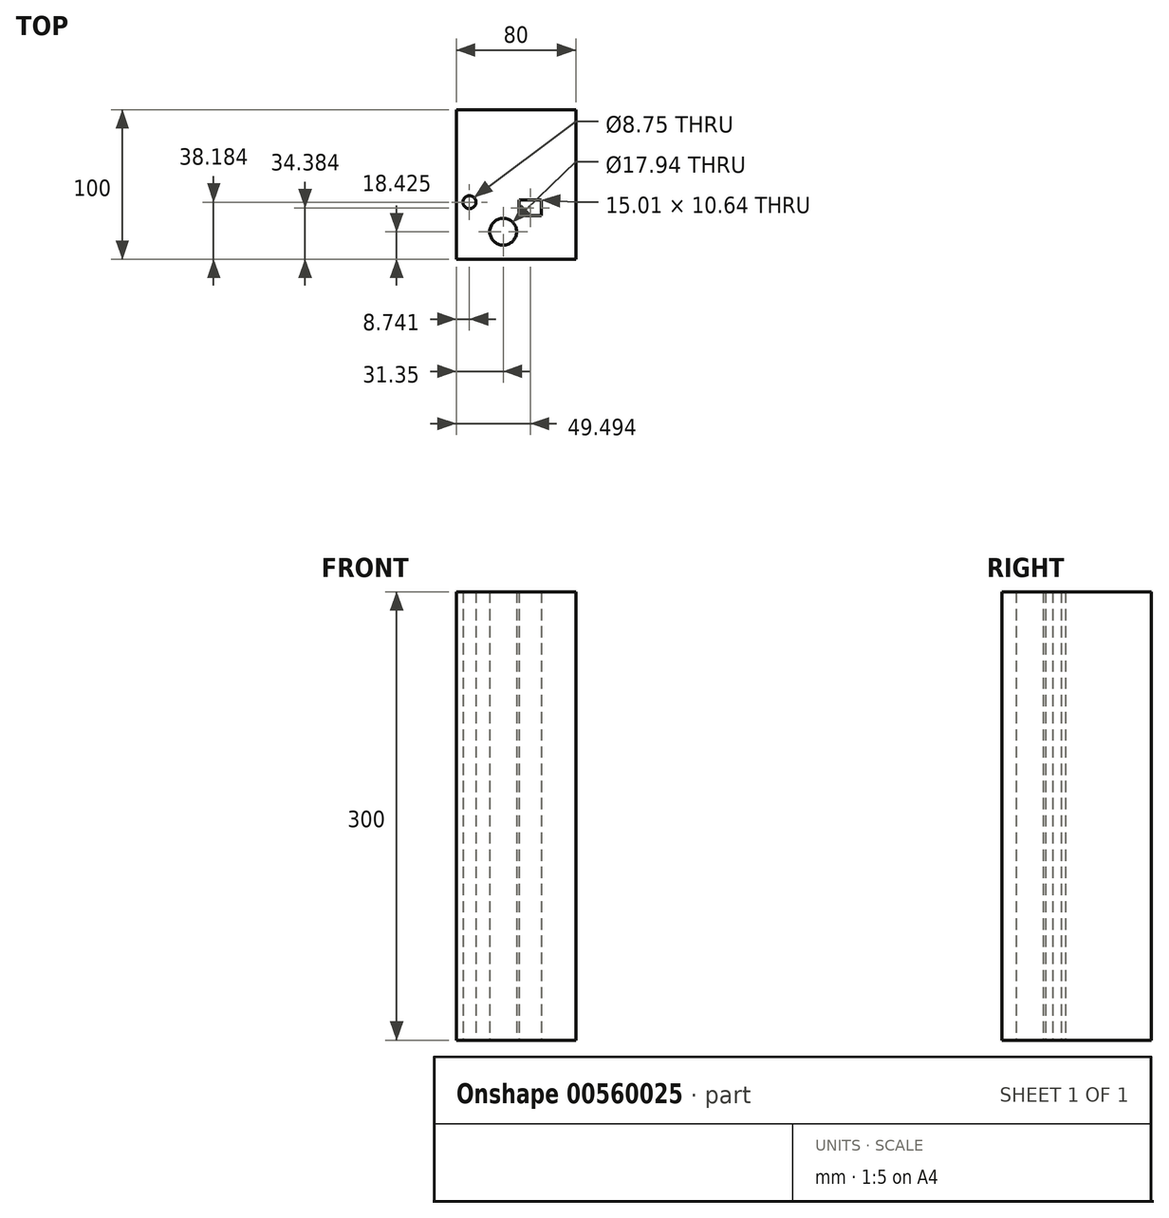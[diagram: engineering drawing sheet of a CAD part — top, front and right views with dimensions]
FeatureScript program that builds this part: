
annotation { "Feature Type Name" : "Feature", "Feature Type Description" : "" }
export const myFeature = defineFeature(function(context is Context, id is Id, definition is map)
    precondition{}
    {
        {
            var Q0;
            Q0=qCreatedBy(makeId("Top.planeOp"),FACE);
            var sketch = newSketch(context, id + "F0", { "sketchPlane" : qUnion([Q0])});
            skLineSegment(sketch, "E0.bottom", {"start": v(-27.74, 75.78) * mm, "end": v(52.26, 75.78) * mm});
            skLineSegment(sketch, "E0.top", {"start": v(-27.74, -24.22) * mm, "end": v(52.26, -24.22) * mm});
            skLineSegment(sketch, "E0.left", {"start": v(-27.74, 75.78) * mm, "end": v(-27.74, -24.22) * mm});
            skLineSegment(sketch, "E0.right", {"start": v(52.26, 75.78) * mm, "end": v(52.26, -24.22) * mm});
            skCircle(sketch, "E1", {"center": v(-19, 13.96) * mm, "radius": 4.37 * mm});
            skCircle(sketch, "E2", {"center": v(3.6, -5.8) * mm, "radius": 8.97 * mm});
            skLineSegment(sketch, "E3.bottom", {"start": v(14.25, 15.48) * mm, "end": v(29.26, 15.48) * mm});
            skLineSegment(sketch, "E3.top", {"start": v(14.25, 4.84) * mm, "end": v(29.26, 4.84) * mm});
            skLineSegment(sketch, "E3.left", {"start": v(14.25, 15.48) * mm, "end": v(14.25, 4.84) * mm});
            skLineSegment(sketch, "E3.right", {"start": v(29.26, 15.48) * mm, "end": v(29.26, 4.84) * mm});
            skSolve(sketch);
        }
        {
            var Q0;
            Q0=makeQuery(id+"F0.imprint","IMPRINT",FACE,{"disambiguationData":[TD([[makeQuery(id+"F0.imprint","IMPRINT",EDGE,{"derivedFrom":sQuery(id+"F0.wireOp",EDGE,"E0.bottom")}),-1.0]])]});
            extrude(context, id + "F1", {"entities" : qUnion([Q0]), "depth" : 300 * mm, "offsetDistance" : 25 * mm});
        }
    });
